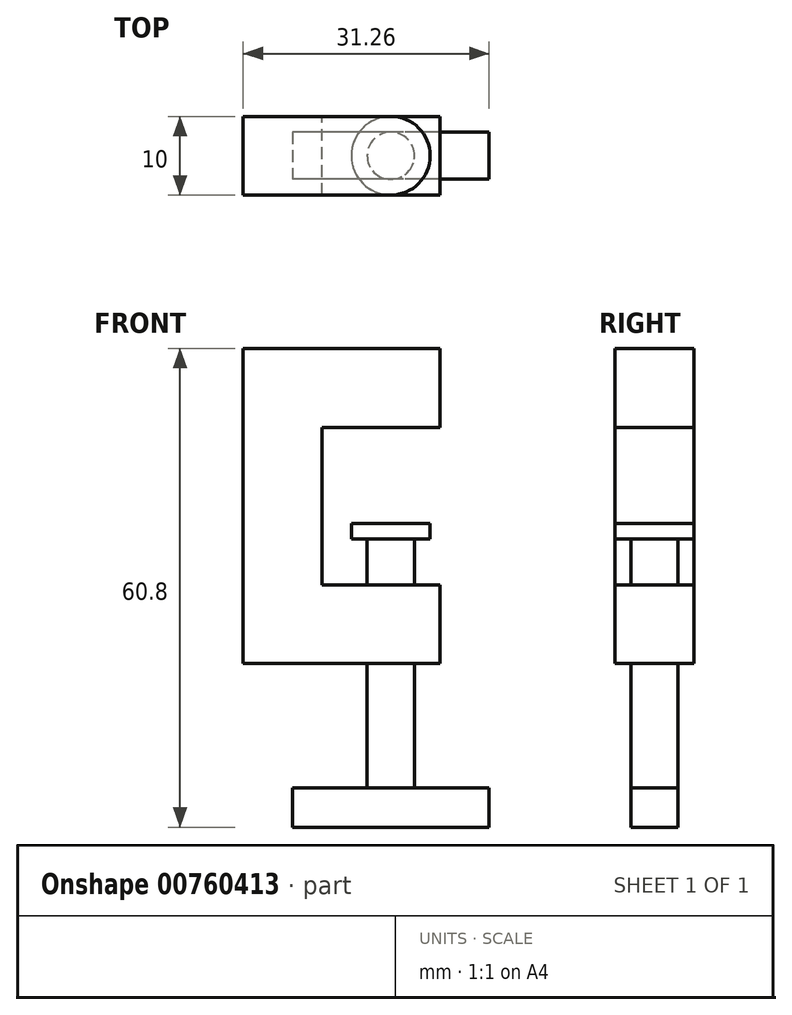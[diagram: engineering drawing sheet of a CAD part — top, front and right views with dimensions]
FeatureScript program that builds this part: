
annotation { "Feature Type Name" : "Feature", "Feature Type Description" : "" }
export const myFeature = defineFeature(function(context is Context, id is Id, definition is map)
    precondition{}
    {
        {
            var Q0;
            Q0=qCreatedBy(makeId("Front.planeOp"),FACE);
            var sketch = newSketch(context, id + "F0", { "sketchPlane" : qUnion([Q0])});
            skLineSegment(sketch, "E0.bottom", {"start": v(0, 0) * mm, "end": v(-10, 0) * mm});
            skLineSegment(sketch, "E0.top", {"start": v(0, 40) * mm, "end": v(-10, 40) * mm});
            skLineSegment(sketch, "E0.left", {"start": v(0, 0) * mm, "end": v(0, 40) * mm});
            skLineSegment(sketch, "E0.right", {"start": v(-10, 0) * mm, "end": v(-10, 40) * mm});
            skLineSegment(sketch, "E1.bottom", {"start": v(0, 0) * mm, "end": v(15, 0) * mm});
            skLineSegment(sketch, "E1.top", {"start": v(0, 10) * mm, "end": v(15, 10) * mm});
            skLineSegment(sketch, "E1.left", {"start": v(0, 0) * mm, "end": v(0, 10) * mm});
            skLineSegment(sketch, "E1.right", {"start": v(15, 0) * mm, "end": v(15, 10) * mm});
            skLineSegment(sketch, "E2.bottom", {"start": v(0, 40) * mm, "end": v(15, 40) * mm});
            skLineSegment(sketch, "E2.top", {"start": v(0, 30) * mm, "end": v(15, 30) * mm});
            skLineSegment(sketch, "E2.left", {"start": v(0, 40) * mm, "end": v(0, 30) * mm});
            skLineSegment(sketch, "E2.right", {"start": v(15, 40) * mm, "end": v(15, 30) * mm});
            skSolve(sketch);
        }
        {
            var Q0;
            Q0 = qSketchRegion(id + "F0", true);
            extrude(context, id + "F1", {"entities" : qUnion([Q0]), "depth" : 10 * mm, "offsetDistance" : 25 * mm});
        }
        {
            var Q0;
            Q0=makeQuery(id+"F1.opExtrude","SWEPT_FACE",FACE,{"disambiguationData":[OSD([sQuery(id+"F0.wireOp",EDGE,"E0.bottom"),sQuery(id+"F0.wireOp",EDGE,"E1.bottom")])]});
            var sketch = newSketch(context, id + "F2", { "sketchPlane" : qUnion([Q0])});
            skCircle(sketch, "E3", {"center": v(8.76, 5) * mm, "radius": 3 * mm});
            skPoint(sketch, "E3.centerSnap0", {"position": v(15, 5) * mm});
            skSolve(sketch);
        }
        {
            var Q0;
            Q0=makeQuery(id+"F2.imprint","IMPRINT",FACE,{"disambiguationData":[TD([[makeQuery(id+"F2.imprint","IMPRINT",EDGE,{"derivedFrom":sQuery(id+"F2.wireOp",EDGE,"E3")}),1.0]])]});
            extrude(context, id + "F3", {"entities" : qUnion([Q0]), "operationType" : NewBodyOperationType.ADD, "endBound" : BoundingType.SYMMETRIC, "oppositeDirection" : true, "depth" : 31.6 * mm, "offsetDistance" : 25 * mm});
        }
        {
            var Q0;
            Q0=makeQuery(id+"F3.opExtrude","CAP_FACE",FACE,{"disambiguationData":[OSD([sQuery(id+"F2.wireOp",EDGE,"E3")])],"isStart":true});
            var sketch = newSketch(context, id + "F4", { "sketchPlane" : qUnion([Q0])});
            skLineSegment(sketch, "E4.bottom", {"start": v(21.26, 2) * mm, "end": v(-3.74, 2) * mm});
            skLineSegment(sketch, "E4.top", {"start": v(21.26, 8) * mm, "end": v(-3.74, 8) * mm});
            skLineSegment(sketch, "E4.left", {"start": v(21.26, 2) * mm, "end": v(21.26, 8) * mm});
            skLineSegment(sketch, "E4.right", {"start": v(-3.74, 2) * mm, "end": v(-3.74, 8) * mm});
            skPoint(sketch, "E4.middle", {"position": v(8.76, 5) * mm});
            skSolve(sketch);
        }
        {
            var Q0;
            {var subQ0=sQuery(id+"F4.wireOp",EDGE,"E4.right");Q0=makeQuery(id+"F4.imprint","IMPRINT",FACE,{"disambiguationData":[TD([[makeQuery(id+"F4.imprint","IMPRINT",EDGE,{"derivedFrom":subQ0}),-1.0]])]});}
            var Q1;
            {var subQ0=sQuery(id+"F4.wireOp",EDGE,"E4.left");Q1=makeQuery(id+"F4.imprint","IMPRINT",FACE,{"disambiguationData":[TD([[makeQuery(id+"F4.imprint","IMPRINT",EDGE,{"derivedFrom":subQ0}),1.0]])]});}
            var Q2;
            {var subQ0=makeQuery(id+"F3.opExtrude","CAP_EDGE",EDGE,{"disambiguationData":[OSD([sQuery(id+"F2.wireOp",EDGE,"E3")])],"isStart":true});var subQ1=makeQuery(id+"F4.imprint","INTERSECT",VERTEX,{"derivedFrom":[subQ0,sQuery(id+"F4.wireOp",EDGE,"E4.bottom")]});Q2=makeQuery(id+"F4.imprint","IMPRINT",FACE,{"disambiguationData":[TD([[makeQuery(id+"F4.imprint","IMPRINT",EDGE,{"disambiguationData":[TD([[subQ1,-1.0]])],"derivedFrom":subQ0}),1.0]])]});}
            extrude(context, id + "F5", {"entities" : qUnion([Q0, Q1, Q2]), "operationType" : NewBodyOperationType.ADD, "depth" : 5 * mm, "offsetDistance" : 25 * mm});
        }
        {
            var Q0;
            Q0=makeQuery(id+"F3.opExtrude","CAP_FACE",FACE,{"disambiguationData":[OSD([sQuery(id+"F2.wireOp",EDGE,"E3")])],"isStart":false});
            var sketch = newSketch(context, id + "F6", { "sketchPlane" : qUnion([Q0])});
            skCircle(sketch, "E5", {"center": v(8.76, -5) * mm, "radius": 5 * mm});
            skSolve(sketch);
        }
        {
            var Q0;
            Q0=makeQuery(id+"F6.imprint","IMPRINT",FACE,{"disambiguationData":[TD([[makeQuery(id+"F6.imprint","IMPRINT",EDGE,{"derivedFrom":sQuery(id+"F6.wireOp",EDGE,"E5")}),1.0]])]});
            var Q1;
            Q1=makeQuery(id+"F6.imprint","IMPRINT",FACE,{"disambiguationData":[TD([[makeQuery(id+"F6.imprint","IMPRINT",EDGE,{"derivedFrom":makeQuery(id+"F3.opExtrude","CAP_EDGE",EDGE,{"disambiguationData":[OSD([sQuery(id+"F2.wireOp",EDGE,"E3")])],"isStart":false})}),-1.0]])]});
            extrude(context, id + "F7", {"entities" : qUnion([Q0, Q1]), "operationType" : NewBodyOperationType.ADD, "depth" : 2 * mm, "offsetDistance" : 25 * mm});
        }
    });
